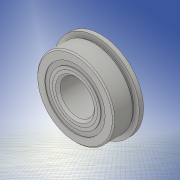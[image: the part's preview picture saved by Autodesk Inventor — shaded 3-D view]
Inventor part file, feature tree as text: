
AUTODESK INVENTOR PART (.ipt)
format: ipt  version: 2016 (Build 200138000, 138)  size: 625,664 bytes
history: native  units: in
note: dims shown in document units (in); Inventor stores cm internally (conversion verified against a paired STEP export)
features: other x12, revolve x5
ambient origin geometry x8: Origin, YZ Plane, XZ Plane, XY Plane, X Axis, Y Axis, Z Axis, Center Point
bodies: Solid1 (feature_tree), Solid2 (feature_tree), Solid3 (feature_tree), Solid4 (feature_tree), Solid5 (feature_tree), Solid6 (feature_tree), Solid7 (feature_tree), Solid8 (feature_tree), Solid9 (feature_tree), Solid10 (feature_tree), Solid11 (feature_tree), Solid12 (feature_tree), Solid13 (feature_tree), Solid14 (feature_tree), Solid15 (feature_tree), Solid16 (feature_tree), Solid17 (feature_tree)
feature tree (17):
  revolve  "Revolve2"  [1 undecoded]
  revolve  "Revolve3"  [1 undecoded]
  other  "Cut-Revolve1"
  revolve  "Revolve4"  [1 undecoded]
  other  "CirPattern1[1]"
  other  "CirPattern1[2]"
  other  "CirPattern1[3]"
  other  "CirPattern1[4]"
  other  "CirPattern1[5]"
  other  "CirPattern1[6]"
  other  "CirPattern1[7]"
  other  "CirPattern1[8]"
  other  "CirPattern1[9]"
  other  "CirPattern1[10]"
  other  "CirPattern1[11]"
  revolve  "Revolve6[1]"  [1 undecoded]
  revolve  "Revolve6[2]"  [1 undecoded]
note: 5 required parameter values undecoded (feature->parameter linkage not recoverable at this tier; creation-order binding heuristic only, values carry confidence <= 0.55)
